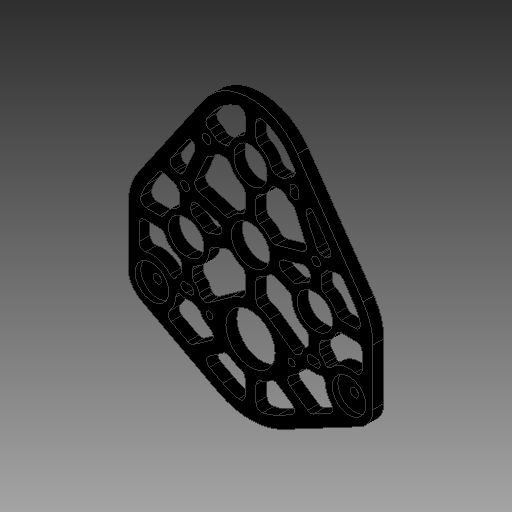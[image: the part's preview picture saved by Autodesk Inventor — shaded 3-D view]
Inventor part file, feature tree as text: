
AUTODESK INVENTOR PART (.ipt)
format: ipt  version: 2019 (Build 230136000, 136)  size: 518,656 bytes
history: native  units: in
note: dims shown in document units (in); Inventor stores cm internally (conversion verified against a paired STEP export)
features: fillet x1
ambient origin geometry x8: Origin, YZ Plane, XZ Plane, XY Plane, X Axis, Y Axis, Z Axis, Center Point
bodies: Solid1 (feature_tree)
feature tree (1):
  fillet  "Fillet68"  [1 undecoded]
note: 1 required parameter value undecoded (feature->parameter linkage not recoverable at this tier; creation-order binding heuristic only, values carry confidence <= 0.55)
